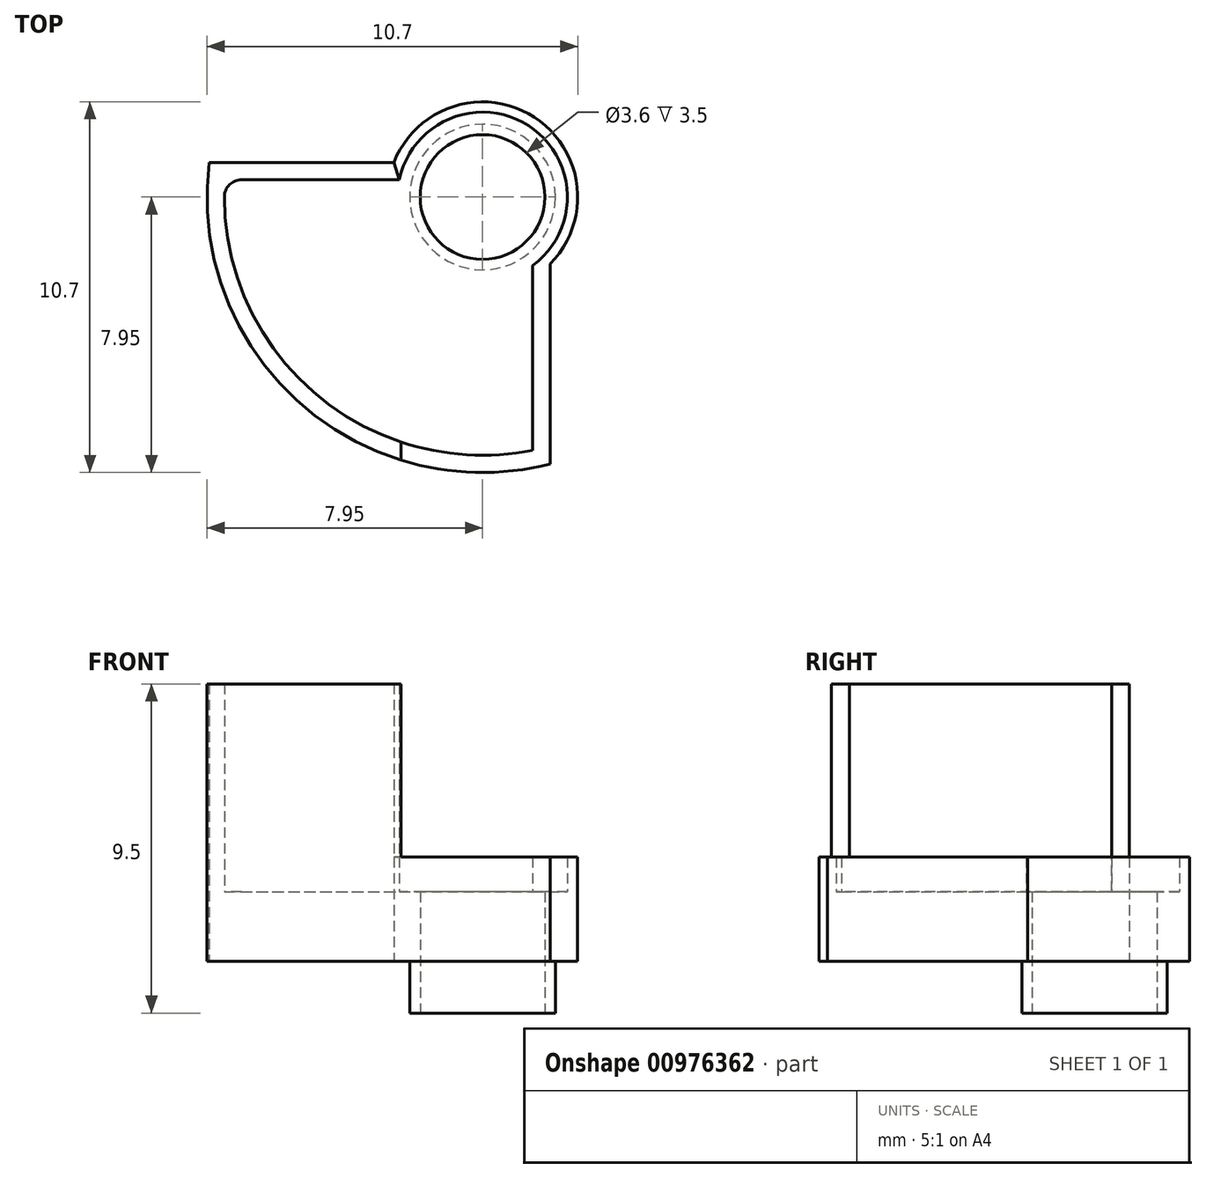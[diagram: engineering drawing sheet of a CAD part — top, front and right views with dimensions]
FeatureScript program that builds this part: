
annotation { "Feature Type Name" : "Feature", "Feature Type Description" : "" }
export const myFeature = defineFeature(function(context is Context, id is Id, definition is map)
    precondition{}
    {
        {
            var Q0;
            Q0=qCreatedBy(makeId("Top.planeOp"),FACE);
            var sketch = newSketch(context, id + "F0", { "sketchPlane" : qUnion([Q0])});
            skCircle(sketch, "E0", {"center": v(0, 0) * mm, "radius": 2.45 * mm});
            skCircle(sketch, "E1", {"center": v(0, 0) * mm, "radius": 2.75 * mm});
            skLineSegment(sketch, "E2", {"start": v(0, 0) * mm, "end": v(0, 1) * mm});
            skCircle(sketch, "E3", {"center": v(0, 0) * mm, "radius": 7.95 * mm});
            skLineSegment(sketch, "E4", {"start": v(0, 1) * mm, "end": v(-7.89, 1) * mm});
            skLineSegment(sketch, "E5", {"start": v(0, 0) * mm, "end": v(-7.95, 0) * mm});
            skPoint(sketch, "E6", {"position": v(-1, 1) * mm});
            skLineSegment(sketch, "E7", {"start": v(0, 0) * mm, "end": v(2.45, 0) * mm});
            skLineSegment(sketch, "E8", {"start": v(1.45, 0) * mm, "end": v(1.45, -7.82) * mm});
            skLineSegment(sketch, "E9", {"start": v(1.45, 0) * mm, "end": v(0.88, 0) * mm});
            skLineSegment(sketch, "E10", {"start": v(1.45, 0) * mm, "end": v(1.95, 0) * mm});
            skPoint(sketch, "E11", {"position": v(1.95, 0) * mm});
            skLineSegment(sketch, "E12", {"start": v(1.95, 0) * mm, "end": v(1.95, -7.7) * mm});
            skCircle(sketch, "E13", {"center": v(0, 0) * mm, "radius": 7.45 * mm});
            skPoint(sketch, "E14", {"position": v(0, 0.5) * mm});
            skLineSegment(sketch, "E15", {"start": v(0, 0.5) * mm, "end": v(-7.93, 0.5) * mm});
            skCircle(sketch, "E16", {"center": v(0, 0) * mm, "radius": 2.1 * mm});
            skCircle(sketch, "E17", {"center": v(0, 0) * mm, "radius": 1.8 * mm});
            skSolve(sketch);
        }
        {
            var Q0;
            {var subQ0=sQuery(id+"F0.wireOp",EDGE,"E4");var subQ1=sQuery(id+"F0.wireOp",EDGE,"E0");var subQ2=makeQuery(id+"F0.imprint","INTERSECT",VERTEX,{"derivedFrom":[subQ1,subQ0]});Q0=makeQuery(id+"F0.imprint","IMPRINT",FACE,{"disambiguationData":[TD([[makeQuery(id+"F0.imprint","IMPRINT",EDGE,{"disambiguationData":[TD([[subQ2,-1.0]])],"derivedFrom":subQ1}),-1.0]])]});}
            var Q1;
            {var subQ0=sQuery(id+"F0.wireOp",EDGE,"E4");var subQ1=sQuery(id+"F0.wireOp",EDGE,"E0");var subQ2=makeQuery(id+"F0.imprint","INTERSECT",VERTEX,{"derivedFrom":[subQ1,subQ0]});Q1=makeQuery(id+"F0.imprint","IMPRINT",FACE,{"disambiguationData":[TD([[makeQuery(id+"F0.imprint","IMPRINT",EDGE,{"disambiguationData":[TD([[subQ2,1.0]])],"derivedFrom":subQ1}),-1.0]])]});}
            var Q2;
            {var subQ0=sQuery(id+"F0.wireOp",EDGE,"E4");var subQ1=sQuery(id+"F0.wireOp",EDGE,"E1");var subQ2=makeQuery(id+"F0.imprint","INTERSECT",VERTEX,{"derivedFrom":[subQ1,subQ0]});Q2=makeQuery(id+"F0.imprint","IMPRINT",FACE,{"disambiguationData":[TD([[makeQuery(id+"F0.imprint","IMPRINT",EDGE,{"disambiguationData":[TD([[subQ2,-1.0]])],"derivedFrom":subQ1}),-1.0]])]});}
            var Q3;
            {var subQ0=sQuery(id+"F0.wireOp",EDGE,"IF1eqrjG-gs3F-z6uJ-pAVS-guX6vDJRSqos");var subQ1=sQuery(id+"F0.wireOp",EDGE,"E0");var subQ2=makeQuery(id+"F0.imprint","INTERSECT",VERTEX,{"derivedFrom":[subQ1,subQ0]});Q3=makeQuery(id+"F0.imprint","IMPRINT",FACE,{"disambiguationData":[TD([[makeQuery(id+"F0.imprint","IMPRINT",EDGE,{"disambiguationData":[TD([[subQ2,-1.0]])],"derivedFrom":subQ1}),-1.0]])]});}
            var Q4;
            {var subQ0=sQuery(id+"F0.wireOp",EDGE,"E5");var subQ1=sQuery(id+"F0.wireOp",EDGE,"E1");var subQ2=makeQuery(id+"F0.imprint","INTERSECT",VERTEX,{"derivedFrom":[subQ1,subQ0]});Q4=makeQuery(id+"F0.imprint","IMPRINT",FACE,{"disambiguationData":[TD([[makeQuery(id+"F0.imprint","IMPRINT",EDGE,{"disambiguationData":[TD([[subQ2,1.0]])],"derivedFrom":subQ1}),-1.0]])]});}
            var Q5;
            {var subQ0=sQuery(id+"F0.wireOp",EDGE,"E5");var subQ1=sQuery(id+"F0.wireOp",EDGE,"E1");var subQ2=makeQuery(id+"F0.imprint","INTERSECT",VERTEX,{"derivedFrom":[subQ1,subQ0]});Q5=makeQuery(id+"F0.imprint","IMPRINT",FACE,{"disambiguationData":[TD([[makeQuery(id+"F0.imprint","IMPRINT",EDGE,{"disambiguationData":[TD([[subQ2,-1.0]])],"derivedFrom":subQ1}),-1.0]])]});}
            var Q6;
            {var subQ0=sQuery(id+"F0.wireOp",EDGE,"E5");var subQ1=sQuery(id+"F0.wireOp",EDGE,"E0");var subQ2=makeQuery(id+"F0.imprint","INTERSECT",VERTEX,{"derivedFrom":[subQ1,subQ0]});Q6=makeQuery(id+"F0.imprint","IMPRINT",FACE,{"disambiguationData":[TD([[makeQuery(id+"F0.imprint","IMPRINT",EDGE,{"disambiguationData":[TD([[subQ2,-1.0]])],"derivedFrom":subQ1}),-1.0]])]});}
            var Q7;
            {var subQ0=sQuery(id+"F0.wireOp",EDGE,"ne5v6ABM-PLVu-a9V9-Vy7H-CvR2PCioNrc4");var subQ1=sQuery(id+"F0.wireOp",EDGE,"E0");var subQ2=makeQuery(id+"F0.imprint","INTERSECT",VERTEX,{"derivedFrom":[subQ1,subQ0]});Q7=makeQuery(id+"F0.imprint","IMPRINT",FACE,{"disambiguationData":[TD([[makeQuery(id+"F0.imprint","IMPRINT",EDGE,{"disambiguationData":[TD([[subQ2,-1.0]])],"derivedFrom":subQ1}),-1.0]])]});}
            var Q8;
            {var subQ0=sQuery(id+"F0.wireOp",EDGE,"kMcXOdmb-bVyM-Q9BF-ijKS-k2YpHzg6PhCW");var subQ1=sQuery(id+"F0.wireOp",EDGE,"E0");var subQ2=makeQuery(id+"F0.imprint","INTERSECT",VERTEX,{"derivedFrom":[subQ1,subQ0]});Q8=makeQuery(id+"F0.imprint","IMPRINT",FACE,{"disambiguationData":[TD([[makeQuery(id+"F0.imprint","IMPRINT",EDGE,{"disambiguationData":[TD([[subQ2,-1.0]])],"derivedFrom":subQ1}),-1.0]])]});}
            var Q9;
            {var subQ0=sQuery(id+"F0.wireOp",EDGE,"E8");var subQ1=sQuery(id+"F0.wireOp",EDGE,"E0");var subQ2=makeQuery(id+"F0.imprint","INTERSECT",VERTEX,{"derivedFrom":[subQ1,subQ0]});Q9=makeQuery(id+"F0.imprint","IMPRINT",FACE,{"disambiguationData":[TD([[makeQuery(id+"F0.imprint","IMPRINT",EDGE,{"disambiguationData":[TD([[subQ2,-1.0]])],"derivedFrom":subQ1}),-1.0]])]});}
            var Q10;
            {var subQ0=sQuery(id+"F0.wireOp",EDGE,"E5");var subQ1=sQuery(id+"F0.wireOp",EDGE,"E1");var subQ2=makeQuery(id+"F0.imprint","INTERSECT",VERTEX,{"derivedFrom":[subQ1,subQ0]});Q10=makeQuery(id+"F0.imprint","IMPRINT",FACE,{"disambiguationData":[TD([[makeQuery(id+"F0.imprint","IMPRINT",EDGE,{"disambiguationData":[TD([[subQ2,1.0]])],"derivedFrom":subQ1}),-1.0]])]});}
            var Q11;
            {var subQ0=sQuery(id+"F0.wireOp",EDGE,"E5");var subQ1=sQuery(id+"F0.wireOp",EDGE,"E1");var subQ2=makeQuery(id+"F0.imprint","INTERSECT",VERTEX,{"derivedFrom":[subQ1,subQ0]});Q11=makeQuery(id+"F0.imprint","IMPRINT",FACE,{"disambiguationData":[TD([[makeQuery(id+"F0.imprint","IMPRINT",EDGE,{"disambiguationData":[TD([[subQ2,-1.0]])],"derivedFrom":subQ1}),-1.0]])]});}
            var Q12;
            {var subQ0=sQuery(id+"F0.wireOp",EDGE,"E8");var subQ1=sQuery(id+"F0.wireOp",EDGE,"E1");var subQ2=makeQuery(id+"F0.imprint","INTERSECT",VERTEX,{"derivedFrom":[subQ1,subQ0]});Q12=makeQuery(id+"F0.imprint","IMPRINT",FACE,{"disambiguationData":[TD([[makeQuery(id+"F0.imprint","IMPRINT",EDGE,{"disambiguationData":[TD([[subQ2,-1.0]])],"derivedFrom":subQ1}),-1.0]])]});}
            var Q13;
            {var subQ0=sQuery(id+"F0.wireOp",EDGE,"E4");var subQ1=sQuery(id+"F0.wireOp",EDGE,"E3");var subQ2=makeQuery(id+"F0.imprint","INTERSECT",VERTEX,{"derivedFrom":[subQ1,subQ0]});Q13=makeQuery(id+"F0.imprint","IMPRINT",FACE,{"disambiguationData":[TD([[makeQuery(id+"F0.imprint","IMPRINT",EDGE,{"disambiguationData":[TD([[subQ2,-1.0]])],"derivedFrom":subQ1}),1.0]])]});}
            var Q14;
            {var subQ0=sQuery(id+"F0.wireOp",EDGE,"E8");var subQ1=sQuery(id+"F0.wireOp",EDGE,"E3");var subQ2=makeQuery(id+"F0.imprint","INTERSECT",VERTEX,{"derivedFrom":[subQ1,subQ0]});Q14=makeQuery(id+"F0.imprint","IMPRINT",FACE,{"disambiguationData":[TD([[makeQuery(id+"F0.imprint","IMPRINT",EDGE,{"disambiguationData":[TD([[subQ2,-1.0]])],"derivedFrom":subQ1}),1.0]])]});}
            var Q15;
            {var subQ0=sQuery(id+"F0.wireOp",EDGE,"E5");var subQ1=sQuery(id+"F0.wireOp",EDGE,"E1");var subQ2=makeQuery(id+"F0.imprint","INTERSECT",VERTEX,{"derivedFrom":[subQ1,subQ0]});Q15=makeQuery(id+"F0.imprint","IMPRINT",FACE,{"disambiguationData":[TD([[makeQuery(id+"F0.imprint","IMPRINT",EDGE,{"disambiguationData":[TD([[subQ2,1.0]])],"derivedFrom":subQ1}),-1.0]])]});}
            var Q16;
            {var subQ0=sQuery(id+"F0.wireOp",EDGE,"E5");var subQ1=sQuery(id+"F0.wireOp",EDGE,"E1");var subQ2=makeQuery(id+"F0.imprint","INTERSECT",VERTEX,{"derivedFrom":[subQ1,subQ0]});Q16=makeQuery(id+"F0.imprint","IMPRINT",FACE,{"disambiguationData":[TD([[makeQuery(id+"F0.imprint","IMPRINT",EDGE,{"disambiguationData":[TD([[subQ2,-1.0]])],"derivedFrom":subQ1}),-1.0]])]});}
            var Q17;
            {var subQ0=sQuery(id+"F0.wireOp",EDGE,"E8");var subQ1=sQuery(id+"F0.wireOp",EDGE,"E1");var subQ2=makeQuery(id+"F0.imprint","INTERSECT",VERTEX,{"derivedFrom":[subQ1,subQ0]});Q17=makeQuery(id+"F0.imprint","IMPRINT",FACE,{"disambiguationData":[TD([[makeQuery(id+"F0.imprint","IMPRINT",EDGE,{"disambiguationData":[TD([[subQ2,-1.0]])],"derivedFrom":subQ1}),-1.0]])]});}
            var Q18;
            {var subQ0=sQuery(id+"F0.wireOp",EDGE,"E4");var subQ1=sQuery(id+"F0.wireOp",EDGE,"E3");var subQ2=makeQuery(id+"F0.imprint","INTERSECT",VERTEX,{"derivedFrom":[subQ1,subQ0]});Q18=makeQuery(id+"F0.imprint","IMPRINT",FACE,{"disambiguationData":[TD([[makeQuery(id+"F0.imprint","IMPRINT",EDGE,{"disambiguationData":[TD([[subQ2,-1.0]])],"derivedFrom":subQ1}),1.0]])]});}
            var Q19;
            {var subQ0=sQuery(id+"F0.wireOp",EDGE,"E5");var subQ1=sQuery(id+"F0.wireOp",EDGE,"E3");var subQ2=makeQuery(id+"F0.imprint","INTERSECT",VERTEX,{"derivedFrom":[subQ1,subQ0]});Q19=makeQuery(id+"F0.imprint","IMPRINT",FACE,{"disambiguationData":[TD([[makeQuery(id+"F0.imprint","IMPRINT",EDGE,{"disambiguationData":[TD([[subQ2,-1.0]])],"derivedFrom":subQ1}),1.0]])]});}
            var Q20;
            {var subQ0=sQuery(id+"F0.wireOp",EDGE,"E8");var subQ1=sQuery(id+"F0.wireOp",EDGE,"E3");var subQ2=makeQuery(id+"F0.imprint","INTERSECT",VERTEX,{"derivedFrom":[subQ1,subQ0]});Q20=makeQuery(id+"F0.imprint","IMPRINT",FACE,{"disambiguationData":[TD([[makeQuery(id+"F0.imprint","IMPRINT",EDGE,{"disambiguationData":[TD([[subQ2,-1.0]])],"derivedFrom":subQ1}),1.0]])]});}
            var Q21;
            {var subQ0=sQuery(id+"F0.wireOp",EDGE,"E5");var subQ1=sQuery(id+"F0.wireOp",EDGE,"E3");var subQ2=makeQuery(id+"F0.imprint","INTERSECT",VERTEX,{"derivedFrom":[subQ1,subQ0]});Q21=makeQuery(id+"F0.imprint","IMPRINT",FACE,{"disambiguationData":[TD([[makeQuery(id+"F0.imprint","IMPRINT",EDGE,{"disambiguationData":[TD([[subQ2,1.0]])],"derivedFrom":subQ1}),1.0]])]});}
            var Q22;
            {var subQ0=sQuery(id+"F0.wireOp",EDGE,"E15");var subQ1=sQuery(id+"F0.wireOp",EDGE,"E0");var subQ2=makeQuery(id+"F0.imprint","INTERSECT",VERTEX,{"derivedFrom":[subQ1,subQ0]});Q22=makeQuery(id+"F0.imprint","IMPRINT",FACE,{"disambiguationData":[TD([[makeQuery(id+"F0.imprint","IMPRINT",EDGE,{"disambiguationData":[TD([[subQ2,-1.0]])],"derivedFrom":subQ1}),-1.0]])]});}
            var Q23;
            {var subQ0=sQuery(id+"F0.wireOp",EDGE,"E5");var subQ1=sQuery(id+"F0.wireOp",EDGE,"E0");var subQ2=makeQuery(id+"F0.imprint","INTERSECT",VERTEX,{"derivedFrom":[subQ1,subQ0]});Q23=makeQuery(id+"F0.imprint","IMPRINT",FACE,{"disambiguationData":[TD([[makeQuery(id+"F0.imprint","IMPRINT",EDGE,{"disambiguationData":[TD([[subQ2,-1.0]])],"derivedFrom":subQ1}),1.0]])]});}
            var Q24;
            {var subQ0=sQuery(id+"F0.wireOp",EDGE,"E17");var subQ1=sQuery(id+"F0.wireOp",EDGE,"E5");var subQ2=makeQuery(id+"F0.imprint","INTERSECT",VERTEX,{"derivedFrom":[subQ1,subQ0]});Q24=makeQuery(id+"F0.imprint","IMPRINT",FACE,{"disambiguationData":[TD([[makeQuery(id+"F0.imprint","IMPRINT",EDGE,{"disambiguationData":[TD([[subQ2,-1.0]])],"derivedFrom":subQ1}),1.0]])]});}
            var Q25;
            {var subQ0=sQuery(id+"F0.wireOp",EDGE,"E15");var subQ1=sQuery(id+"F0.wireOp",EDGE,"E0");var subQ2=makeQuery(id+"F0.imprint","INTERSECT",VERTEX,{"derivedFrom":[subQ1,subQ0]});Q25=makeQuery(id+"F0.imprint","IMPRINT",FACE,{"disambiguationData":[TD([[makeQuery(id+"F0.imprint","IMPRINT",EDGE,{"disambiguationData":[TD([[subQ2,-1.0]])],"derivedFrom":subQ1}),1.0]])]});}
            var Q26;
            {var subQ0=sQuery(id+"F0.wireOp",EDGE,"E4");var subQ1=sQuery(id+"F0.wireOp",EDGE,"E0");var subQ2=makeQuery(id+"F0.imprint","INTERSECT",VERTEX,{"derivedFrom":[subQ1,subQ0]});Q26=makeQuery(id+"F0.imprint","IMPRINT",FACE,{"disambiguationData":[TD([[makeQuery(id+"F0.imprint","IMPRINT",EDGE,{"disambiguationData":[TD([[subQ2,-1.0]])],"derivedFrom":subQ1}),1.0]])]});}
            var Q27;
            {var subQ0=sQuery(id+"F0.wireOp",EDGE,"E7");var subQ1=sQuery(id+"F0.wireOp",EDGE,"E0");var subQ2=makeQuery(id+"F0.imprint","INTERSECT",VERTEX,{"derivedFrom":[subQ1,subQ0]});Q27=makeQuery(id+"F0.imprint","IMPRINT",FACE,{"disambiguationData":[TD([[makeQuery(id+"F0.imprint","IMPRINT",EDGE,{"disambiguationData":[TD([[subQ2,-1.0]])],"derivedFrom":subQ1}),1.0]])]});}
            var Q28;
            {var subQ0=sQuery(id+"F0.wireOp",EDGE,"E17");var subQ1=sQuery(id+"F0.wireOp",EDGE,"E5");var subQ2=makeQuery(id+"F0.imprint","INTERSECT",VERTEX,{"derivedFrom":[subQ1,subQ0]});Q28=makeQuery(id+"F0.imprint","IMPRINT",FACE,{"disambiguationData":[TD([[makeQuery(id+"F0.imprint","IMPRINT",EDGE,{"disambiguationData":[TD([[subQ2,-1.0]])],"derivedFrom":subQ1}),-1.0]])]});}
            var Q29;
            {var subQ0=sQuery(id+"F0.wireOp",EDGE,"E17");var subQ1=sQuery(id+"F0.wireOp",EDGE,"E4");var subQ2=makeQuery(id+"F0.imprint","INTERSECT",VERTEX,{"derivedFrom":[subQ1,subQ0]});Q29=makeQuery(id+"F0.imprint","IMPRINT",FACE,{"disambiguationData":[TD([[makeQuery(id+"F0.imprint","IMPRINT",EDGE,{"disambiguationData":[TD([[subQ2,-1.0]])],"derivedFrom":subQ1}),1.0]])]});}
            var Q30;
            {var subQ1=sQuery(id+"F0.wireOp",EDGE,"E4");var subQ7=sQuery(id+"F0.wireOp",EDGE,"E17");var subQ9=makeQuery(id+"F0.imprint","INTERSECT",VERTEX,{"derivedFrom":[subQ1,subQ7]});Q30=makeQuery(id+"F0.imprint","IMPRINT",FACE,{"disambiguationData":[TD([[makeQuery(id+"F0.imprint","IMPRINT",EDGE,{"disambiguationData":[TD([[subQ9,-1.0]])],"derivedFrom":subQ1}),-1.0]])]});}
            var Q31;
            {var subQ1=sQuery(id+"F0.wireOp",EDGE,"E8");var subQ7=sQuery(id+"F0.wireOp",EDGE,"E17");var subQ9=makeQuery(id+"F0.imprint","INTERSECT",VERTEX,{"derivedFrom":[subQ1,subQ7]});Q31=makeQuery(id+"F0.imprint","IMPRINT",FACE,{"disambiguationData":[TD([[makeQuery(id+"F0.imprint","IMPRINT",EDGE,{"disambiguationData":[TD([[subQ9,-1.0]])],"derivedFrom":subQ1}),1.0]])]});}
            var Q32;
            {var subQ0=sQuery(id+"F0.wireOp",EDGE,"E8");var subQ1=sQuery(id+"F0.wireOp",EDGE,"E0");var subQ2=makeQuery(id+"F0.imprint","INTERSECT",VERTEX,{"derivedFrom":[subQ1,subQ0]});Q32=makeQuery(id+"F0.imprint","IMPRINT",FACE,{"disambiguationData":[TD([[makeQuery(id+"F0.imprint","IMPRINT",EDGE,{"disambiguationData":[TD([[subQ2,-1.0]])],"derivedFrom":subQ1}),1.0]])]});}
            var Q33;
            {var subQ1=sQuery(id+"F0.wireOp",EDGE,"E7");var subQ3=sQuery(id+"F0.wireOp",EDGE,"E16");var subQ4=makeQuery(id+"F0.imprint","INTERSECT",VERTEX,{"derivedFrom":[subQ1,subQ3]});Q33=makeQuery(id+"F0.imprint","IMPRINT",FACE,{"disambiguationData":[TD([[makeQuery(id+"F0.imprint","IMPRINT",EDGE,{"disambiguationData":[TD([[subQ4,1.0]])],"derivedFrom":subQ3}),1.0]])]});}
            var Q34;
            {var subQ0=sQuery(id+"F0.wireOp",EDGE,"E7");var subQ1=sQuery(id+"F0.wireOp",EDGE,"E0");var subQ2=makeQuery(id+"F0.imprint","INTERSECT",VERTEX,{"derivedFrom":[subQ1,subQ0]});Q34=makeQuery(id+"F0.imprint","IMPRINT",FACE,{"disambiguationData":[TD([[makeQuery(id+"F0.imprint","IMPRINT",EDGE,{"disambiguationData":[TD([[subQ2,1.0]])],"derivedFrom":subQ1}),1.0]])]});}
            extrude(context, id + "F1", {"entities" : qUnion([Q0, Q1, Q2, Q3, Q4, Q5, Q6, Q7, Q8, Q9, Q10, Q11, Q12, Q13, Q14, Q15, Q16, Q17, Q18, Q19, Q20, Q21, Q22, Q23, Q24, Q25, Q26, Q27, Q28, Q29, Q30, Q31, Q32, Q33, Q34]), "depth" : 2 * mm, "offsetDistance" : 25 * mm});
        }
        {
            var Q0;
            {var subQ0=sQuery(id+"F0.wireOp",EDGE,"E4");var subQ1=sQuery(id+"F0.wireOp",EDGE,"E3");var subQ2=makeQuery(id+"F0.imprint","INTERSECT",VERTEX,{"derivedFrom":[subQ1,subQ0]});Q0=makeQuery(id+"F0.imprint","IMPRINT",FACE,{"disambiguationData":[TD([[makeQuery(id+"F0.imprint","IMPRINT",EDGE,{"disambiguationData":[TD([[subQ2,-1.0]])],"derivedFrom":subQ1}),1.0]])]});}
            var Q1;
            {var subQ0=sQuery(id+"F0.wireOp",EDGE,"E15");var subQ1=sQuery(id+"F0.wireOp",EDGE,"E1");var subQ2=makeQuery(id+"F0.imprint","INTERSECT",VERTEX,{"derivedFrom":[subQ1,subQ0]});Q1=makeQuery(id+"F0.imprint","IMPRINT",FACE,{"disambiguationData":[TD([[makeQuery(id+"F0.imprint","IMPRINT",EDGE,{"disambiguationData":[TD([[subQ2,1.0]])],"derivedFrom":subQ1}),-1.0]])]});}
            var Q2;
            {var subQ0=sQuery(id+"F0.wireOp",EDGE,"E4");var subQ1=sQuery(id+"F0.wireOp",EDGE,"E0");var subQ2=makeQuery(id+"F0.imprint","INTERSECT",VERTEX,{"derivedFrom":[subQ1,subQ0]});Q2=makeQuery(id+"F0.imprint","IMPRINT",FACE,{"disambiguationData":[TD([[makeQuery(id+"F0.imprint","IMPRINT",EDGE,{"disambiguationData":[TD([[subQ2,-1.0]])],"derivedFrom":subQ1}),-1.0]])]});}
            var Q3;
            {var subQ1=sQuery(id+"F0.wireOp",EDGE,"E0");var subQ7=makeQuery(id+"F0.imprint","INTERSECT",VERTEX,{"derivedFrom":[subQ1,sQuery(id+"F0.wireOp",EDGE,"E7")]});Q3=makeQuery(id+"F0.imprint","IMPRINT",FACE,{"disambiguationData":[TD([[makeQuery(id+"F0.imprint","IMPRINT",EDGE,{"disambiguationData":[TD([[subQ7,-1.0]])],"derivedFrom":subQ1}),-1.0]])]});}
            var Q4;
            {var subQ0=sQuery(id+"F0.wireOp",EDGE,"E8");var subQ1=sQuery(id+"F0.wireOp",EDGE,"E0");var subQ2=makeQuery(id+"F0.imprint","INTERSECT",VERTEX,{"derivedFrom":[subQ1,subQ0]});Q4=makeQuery(id+"F0.imprint","IMPRINT",FACE,{"disambiguationData":[TD([[makeQuery(id+"F0.imprint","IMPRINT",EDGE,{"disambiguationData":[TD([[subQ2,-1.0]])],"derivedFrom":subQ1}),-1.0]])]});}
            var Q5;
            {var subQ0=sQuery(id+"F0.wireOp",EDGE,"E8");var subQ1=sQuery(id+"F0.wireOp",EDGE,"E1");var subQ2=makeQuery(id+"F0.imprint","INTERSECT",VERTEX,{"derivedFrom":[subQ1,subQ0]});Q5=makeQuery(id+"F0.imprint","IMPRINT",FACE,{"disambiguationData":[TD([[makeQuery(id+"F0.imprint","IMPRINT",EDGE,{"disambiguationData":[TD([[subQ2,-1.0]])],"derivedFrom":subQ1}),-1.0]])]});}
            var Q6;
            {var subQ0=sQuery(id+"F0.wireOp",EDGE,"E8");var subQ1=sQuery(id+"F0.wireOp",EDGE,"E3");var subQ2=makeQuery(id+"F0.imprint","INTERSECT",VERTEX,{"derivedFrom":[subQ1,subQ0]});Q6=makeQuery(id+"F0.imprint","IMPRINT",FACE,{"disambiguationData":[TD([[makeQuery(id+"F0.imprint","IMPRINT",EDGE,{"disambiguationData":[TD([[subQ2,-1.0]])],"derivedFrom":subQ1}),1.0]])]});}
            var Q7;
            {var subQ0=sQuery(id+"F0.wireOp",EDGE,"E5");var subQ1=sQuery(id+"F0.wireOp",EDGE,"E3");var subQ2=makeQuery(id+"F0.imprint","INTERSECT",VERTEX,{"derivedFrom":[subQ1,subQ0]});Q7=makeQuery(id+"F0.imprint","IMPRINT",FACE,{"disambiguationData":[TD([[makeQuery(id+"F0.imprint","IMPRINT",EDGE,{"disambiguationData":[TD([[subQ2,-1.0]])],"derivedFrom":subQ1}),1.0]])]});}
            var Q8;
            {var subQ0=sQuery(id+"F0.wireOp",EDGE,"E5");var subQ1=sQuery(id+"F0.wireOp",EDGE,"E3");var subQ2=makeQuery(id+"F0.imprint","INTERSECT",VERTEX,{"derivedFrom":[subQ1,subQ0]});Q8=makeQuery(id+"F0.imprint","IMPRINT",FACE,{"disambiguationData":[TD([[makeQuery(id+"F0.imprint","IMPRINT",EDGE,{"disambiguationData":[TD([[subQ2,1.0]])],"derivedFrom":subQ1}),1.0]])]});}
            extrude(context, id + "F2", {"entities" : qUnion([Q0, Q1, Q2, Q3, Q4, Q5, Q6, Q7, Q8]), "operationType" : NewBodyOperationType.ADD, "depth" : 3 * mm, "offsetDistance" : 25 * mm});
        }
        {
            var Q0;
            {var subQ1=sQuery(id+"F0.wireOp",EDGE,"E4");var subQ7=sQuery(id+"F0.wireOp",EDGE,"E17");var subQ9=makeQuery(id+"F0.imprint","INTERSECT",VERTEX,{"derivedFrom":[subQ1,subQ7]});Q0=makeQuery(id+"F0.imprint","IMPRINT",FACE,{"disambiguationData":[TD([[makeQuery(id+"F0.imprint","IMPRINT",EDGE,{"disambiguationData":[TD([[subQ9,-1.0]])],"derivedFrom":subQ1}),-1.0]])]});}
            var Q1;
            {var subQ0=sQuery(id+"F0.wireOp",EDGE,"E17");var subQ1=sQuery(id+"F0.wireOp",EDGE,"E4");var subQ2=makeQuery(id+"F0.imprint","INTERSECT",VERTEX,{"derivedFrom":[subQ1,subQ0]});Q1=makeQuery(id+"F0.imprint","IMPRINT",FACE,{"disambiguationData":[TD([[makeQuery(id+"F0.imprint","IMPRINT",EDGE,{"disambiguationData":[TD([[subQ2,-1.0]])],"derivedFrom":subQ1}),1.0]])]});}
            var Q2;
            {var subQ0=sQuery(id+"F0.wireOp",EDGE,"E17");var subQ1=sQuery(id+"F0.wireOp",EDGE,"E5");var subQ2=makeQuery(id+"F0.imprint","INTERSECT",VERTEX,{"derivedFrom":[subQ1,subQ0]});Q2=makeQuery(id+"F0.imprint","IMPRINT",FACE,{"disambiguationData":[TD([[makeQuery(id+"F0.imprint","IMPRINT",EDGE,{"disambiguationData":[TD([[subQ2,-1.0]])],"derivedFrom":subQ1}),-1.0]])]});}
            var Q3;
            {var subQ0=sQuery(id+"F0.wireOp",EDGE,"E17");var subQ1=sQuery(id+"F0.wireOp",EDGE,"E5");var subQ2=makeQuery(id+"F0.imprint","INTERSECT",VERTEX,{"derivedFrom":[subQ1,subQ0]});Q3=makeQuery(id+"F0.imprint","IMPRINT",FACE,{"disambiguationData":[TD([[makeQuery(id+"F0.imprint","IMPRINT",EDGE,{"disambiguationData":[TD([[subQ2,-1.0]])],"derivedFrom":subQ1}),1.0]])]});}
            var Q4;
            {var subQ1=sQuery(id+"F0.wireOp",EDGE,"E8");var subQ7=sQuery(id+"F0.wireOp",EDGE,"E17");var subQ9=makeQuery(id+"F0.imprint","INTERSECT",VERTEX,{"derivedFrom":[subQ1,subQ7]});Q4=makeQuery(id+"F0.imprint","IMPRINT",FACE,{"disambiguationData":[TD([[makeQuery(id+"F0.imprint","IMPRINT",EDGE,{"disambiguationData":[TD([[subQ9,-1.0]])],"derivedFrom":subQ1}),1.0]])]});}
            var Q5;
            {var subQ1=sQuery(id+"F0.wireOp",EDGE,"E7");var subQ3=sQuery(id+"F0.wireOp",EDGE,"E16");var subQ4=makeQuery(id+"F0.imprint","INTERSECT",VERTEX,{"derivedFrom":[subQ1,subQ3]});Q5=makeQuery(id+"F0.imprint","IMPRINT",FACE,{"disambiguationData":[TD([[makeQuery(id+"F0.imprint","IMPRINT",EDGE,{"disambiguationData":[TD([[subQ4,1.0]])],"derivedFrom":subQ3}),1.0]])]});}
            extrude(context, id + "F3", {"entities" : qUnion([Q0, Q1, Q2, Q3, Q4, Q5]), "operationType" : NewBodyOperationType.ADD, "oppositeDirection" : true, "depth" : 1.5 * mm, "offsetDistance" : 25 * mm});
        }
        {
            var Q0;
            Q0=makeQuery(id+"F2.opExtrude","CAP_FACE",FACE,{"disambiguationData":[OSD([sQuery(id+"F0.wireOp",EDGE,"E0"),sQuery(id+"F0.wireOp",EDGE,"E1"),sQuery(id+"F0.wireOp",EDGE,"E3"),sQuery(id+"F0.wireOp",EDGE,"E4"),sQuery(id+"F0.wireOp",EDGE,"E8"),sQuery(id+"F0.wireOp",EDGE,"E12"),sQuery(id+"F0.wireOp",EDGE,"E13"),sQuery(id+"F0.wireOp",EDGE,"E15")])],"isStart":false});
            var sketch = newSketch(context, id + "F4", { "sketchPlane" : qUnion([Q0])});
            skLineSegment(sketch, "E18", {"start": v(-2.56, 1) * mm, "end": v(-2.4, 0.5) * mm});
            skLineSegment(sketch, "E19", {"start": v(-2.35, -7.07) * mm, "end": v(-2.35, -7.6) * mm});
            skSolve(sketch);
        }
        {
            var Q0;
            Q0=makeQuery(id+"F4.imprint","IMPRINT",FACE,{"disambiguationData":[TD([[makeQuery(id+"F4.imprint","IMPRINT",EDGE,{"derivedFrom":sQuery(id+"F4.wireOp",EDGE,"E18")}),-1.0]])]});
            extrude(context, id + "F5", {"entities" : qUnion([Q0]), "operationType" : NewBodyOperationType.ADD, "depth" : 5 * mm, "offsetDistance" : 25 * mm});
        }
        {
            var Q0;
            {var subQ0=sQuery(id+"F0.wireOp",EDGE,"E15");var subQ1=sQuery(id+"F0.wireOp",EDGE,"E13");Q0=makeQuery(id+"F5.boolean.opBoolean","MERGE",EDGE,{"derivedFrom":[makeQuery(id+"F2.opExtrude","SWEPT_EDGE",EDGE,{"disambiguationData":[OSD([subQ1,subQ0])]}),makeQuery(id+"F5.opExtrude","SWEPT_EDGE",EDGE,{"disambiguationData":[OSD([subQ1,subQ0])]})]});}
            fillet(context, id + "F6", {"entities" : qUnion([Q0]), "radius" : .5 * mm, "tangentPropagation" : true, "allowEdgeOverflow" : false});
        }
    });
